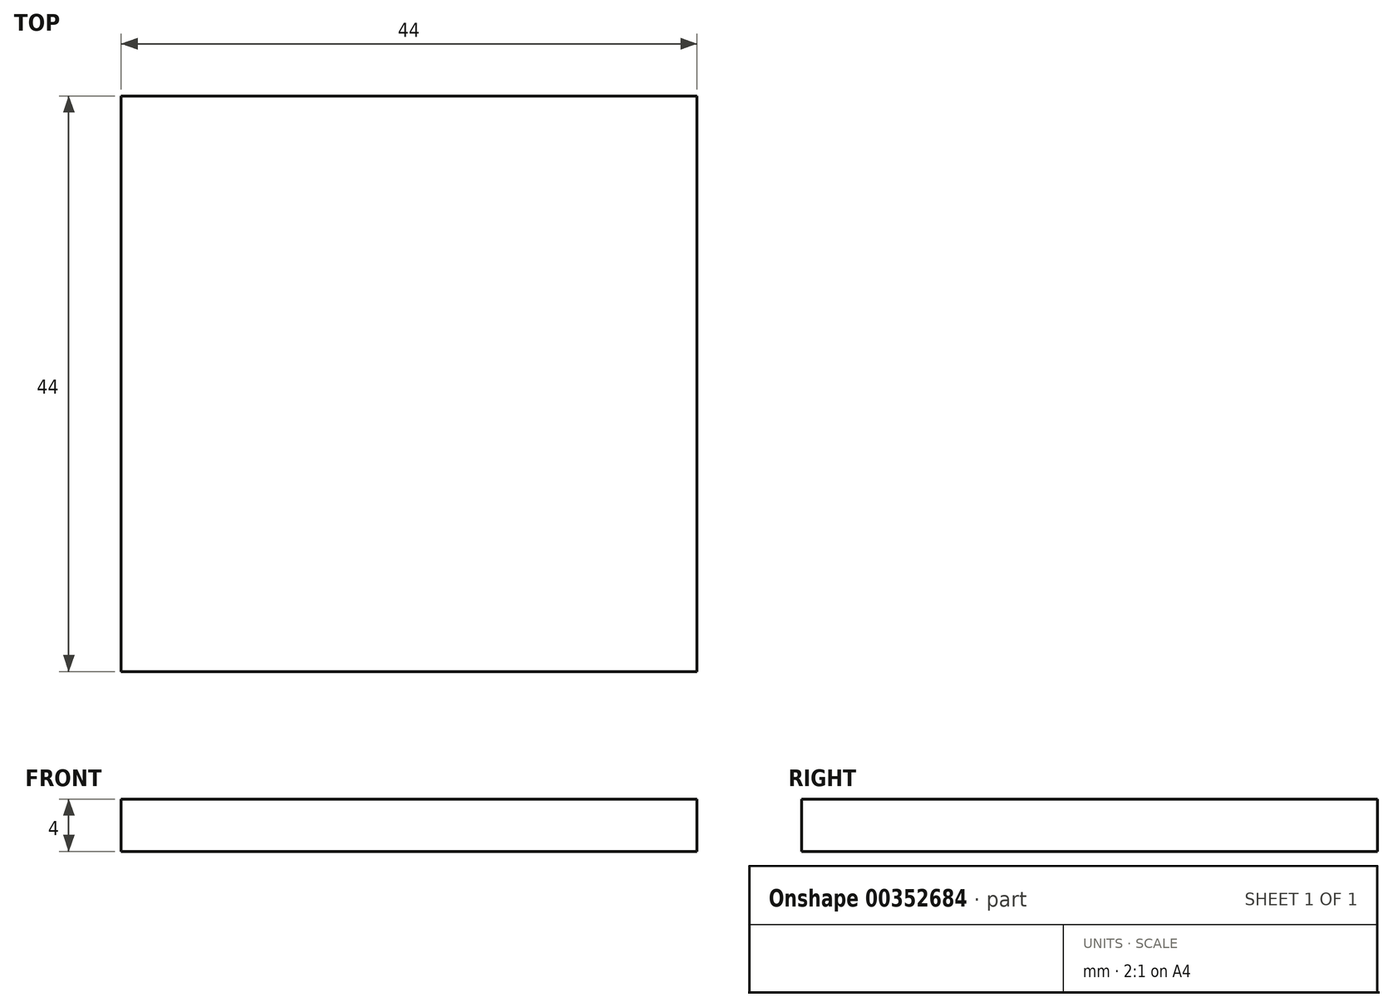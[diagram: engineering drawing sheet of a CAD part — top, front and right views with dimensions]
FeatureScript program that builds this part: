
annotation { "Feature Type Name" : "Feature", "Feature Type Description" : "" }
export const myFeature = defineFeature(function(context is Context, id is Id, definition is map)
    precondition{}
    {
        {
            var Q0;
            Q0=qCreatedBy(makeId("Top.planeOp"),FACE);
            var sketch = newSketch(context, id + "F0", { "sketchPlane" : qUnion([Q0])});
            skLineSegment(sketch, "E0.bottom", {"start": v(-22, 22) * mm, "end": v(22, 22) * mm});
            skLineSegment(sketch, "E0.top", {"start": v(-22, -22) * mm, "end": v(22, -22) * mm});
            skLineSegment(sketch, "E0.left", {"start": v(-22, 22) * mm, "end": v(-22, -22) * mm});
            skLineSegment(sketch, "E0.right", {"start": v(22, 22) * mm, "end": v(22, -22) * mm});
            skPoint(sketch, "E0.middle", {"position": v(0, 0) * mm});
            skSolve(sketch);
        }
        {
            var Q0;
            Q0 = qSketchRegion(id + "F0", true);
            extrude(context, id + "F1", {"entities" : qUnion([Q0]), "depth" : 4 * mm});
        }
    });
